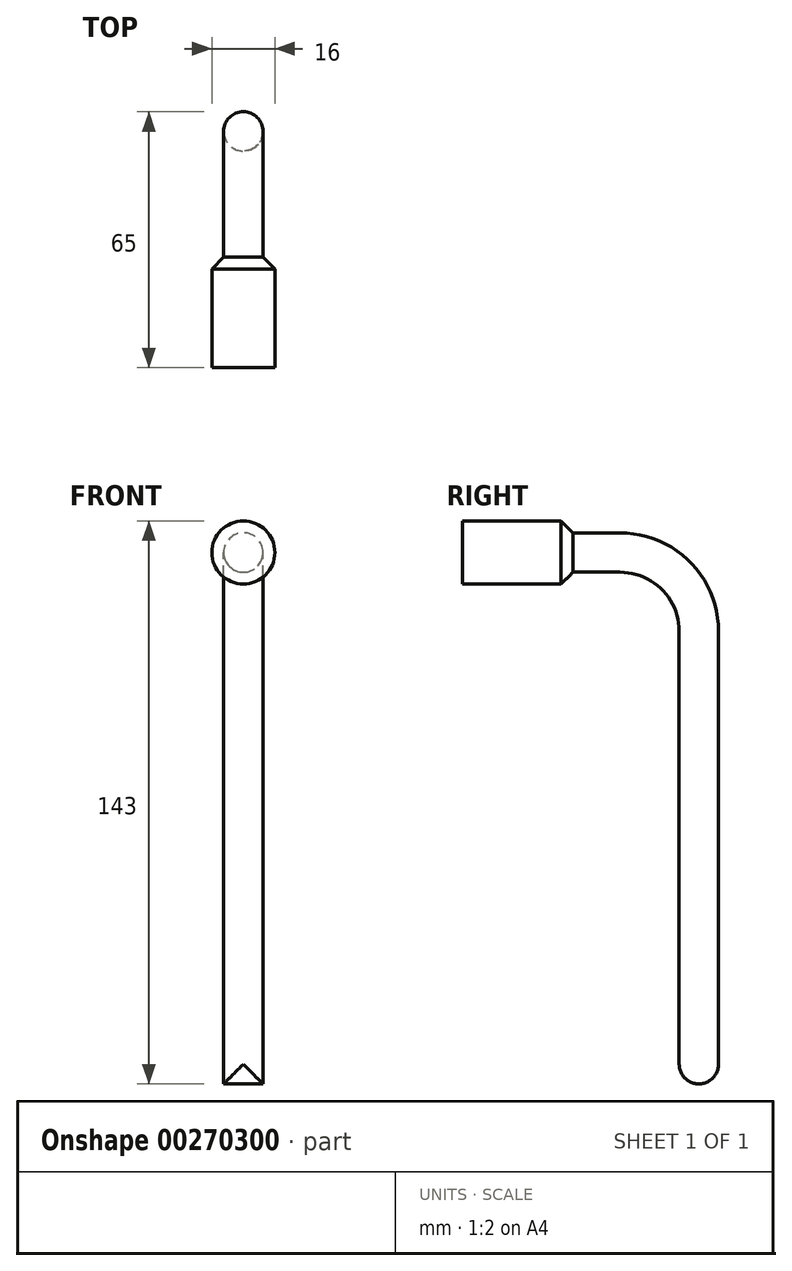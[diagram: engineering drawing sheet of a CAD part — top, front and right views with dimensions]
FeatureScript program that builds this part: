
annotation { "Feature Type Name" : "Feature", "Feature Type Description" : "" }
export const myFeature = defineFeature(function(context is Context, id is Id, definition is map)
    precondition{}
    {
        {
            var Q0;
            Q0=qCreatedBy(makeId("Front.planeOp"),FACE);
            var sketch = newSketch(context, id + "F0", { "sketchPlane" : qUnion([Q0])});
            skLineSegment(sketch, "E0", {"start": v(0, 0) * mm, "end": v(10, 0) * mm});
            skLineSegment(sketch, "E1", {"start": v(10, 0) * mm, "end": v(10, 10) * mm});
            skLineSegment(sketch, "E2", {"start": v(10, 10) * mm, "end": v(0, 10) * mm});
            skLineSegment(sketch, "E3", {"start": v(0, 10) * mm, "end": v(0, 0) * mm});
            skSolve(sketch);
        }
        {
            var Q0;
            Q0 = qSketchRegion(id + "F0", true);
            extrude(context, id + "F1", {"entities" : qUnion([Q0]), "oppositeDirection" : true, "depth" : 65 * mm});
        }
        {
            var Q0;
            Q0=makeQuery(id+"F1.opExtrude","SWEPT_FACE",FACE,{"disambiguationData":[OSD([sQuery(id+"F0.wireOp",EDGE,"E2")])]});
            var sketch = newSketch(context, id + "F2", { "sketchPlane" : qUnion([Q0])});
            skLineSegment(sketch, "E4", {"start": v(0, 65) * mm, "end": v(0, 55) * mm});
            skLineSegment(sketch, "E5", {"start": v(0, 55) * mm, "end": v(10, 55) * mm});
            skLineSegment(sketch, "E6", {"start": v(10, 55) * mm, "end": v(10, 65) * mm});
            skLineSegment(sketch, "E7", {"start": v(10, 65) * mm, "end": v(0, 65) * mm});
            skSolve(sketch);
        }
        {
            var Q0;
            Q0=makeQuery(id+"F2.imprint","IMPRINT",FACE,{"disambiguationData":[TD([[makeQuery(id+"F2.imprint","IMPRINT",EDGE,{"derivedFrom":sQuery(id+"F2.wireOp",EDGE,"E4")}),1.0]])]});
            extrude(context, id + "F3", {"entities" : qUnion([Q0]), "operationType" : NewBodyOperationType.ADD, "oppositeDirection" : true, "depth" : 140 * mm});
        }
        {
            var Q0;
            Q0=makeQuery(id+"F1.opExtrude","CAP_FACE",FACE,{"disambiguationData":[OSD([sQuery(id+"F0.wireOp",EDGE,"E0"),sQuery(id+"F0.wireOp",EDGE,"E1"),sQuery(id+"F0.wireOp",EDGE,"E2"),sQuery(id+"F0.wireOp",EDGE,"E3")])],"isStart":true});
            var sketch = newSketch(context, id + "F4", { "sketchPlane" : qUnion([Q0])});
            skLineSegment(sketch, "E8", {"start": v(0, 0) * mm, "end": v(5, 0) * mm});
            skLineSegment(sketch, "E9", {"start": v(5, 0) * mm, "end": v(5, 5) * mm});
            skCircle(sketch, "E10", {"center": v(5, 5) * mm, "radius": 8 * mm});
            skSolve(sketch);
        }
        {
            var Q0;
            {var subQ2=sQuery(id+"F4.wireOp",EDGE,"E8");Q0=makeQuery(id+"F4.imprint","IMPRINT",FACE,{"disambiguationData":[TD([[makeQuery(id+"F4.imprint","IMPRINT",EDGE,{"derivedFrom":subQ2}),-1.0]])]});}
            extrude(context, id + "F5", {"entities" : qUnion([Q0]), "operationType" : NewBodyOperationType.ADD, "oppositeDirection" : true, "depth" : 30 * mm});
        }
        {
            var Q0;
            Q0=makeQuery(id+"F3.boolean.opBoolean","INTERSECT",EDGE,{"derivedFrom":[makeQuery(id+"F1.opExtrude","SWEPT_FACE",FACE,{"disambiguationData":[OSD([sQuery(id+"F0.wireOp",EDGE,"E0")])]}),makeQuery(id+"F3.opExtrude","SWEPT_FACE",FACE,{"disambiguationData":[OSD([sQuery(id+"F2.wireOp",EDGE,"E5")])]})]});
            fillet(context, id + "F6", {"entities" : qUnion([Q0]), "radius" : 15 * mm, "tangentPropagation" : true, "allowEdgeOverflow" : false});
        }
        {
            var Q0;
            Q0=makeQuery(id+"F1.opExtrude","CAP_EDGE",EDGE,{"disambiguationData":[OSD([sQuery(id+"F0.wireOp",EDGE,"E2")])],"isStart":false});
            fillet(context, id + "F7", {"entities" : qUnion([Q0]), "radius" : 25 * mm, "tangentPropagation" : true, "allowEdgeOverflow" : false});
        }
        {
            var Q0;
            Q0=makeQuery(id+"F3.boolean.opBoolean","MERGE",FACE,{"derivedFrom":[makeQuery(id+"F1.opExtrude","CAP_FACE",FACE,{"disambiguationData":[OSD([sQuery(id+"F0.wireOp",EDGE,"E0"),sQuery(id+"F0.wireOp",EDGE,"E1"),sQuery(id+"F0.wireOp",EDGE,"E2"),sQuery(id+"F0.wireOp",EDGE,"E3")])],"isStart":false}),makeQuery(id+"F3.opExtrude","SWEPT_FACE",FACE,{"disambiguationData":[OSD([sQuery(id+"F2.wireOp",EDGE,"E7")])]})]});
            fillet(context, id + "F8", {"entities" : qUnion([Q0]), "radius" : 5 * mm, "tangentPropagation" : true, "allowEdgeOverflow" : false});
        }
        {
            var Q0;
            Q0=makeQuery(id+"F3.opExtrude","SWEPT_FACE",FACE,{"disambiguationData":[OSD([sQuery(id+"F2.wireOp",EDGE,"E5")])]});
            fillet(context, id + "F9", {"entities" : qUnion([Q0]), "radius" : 5 * mm, "tangentPropagation" : true, "allowEdgeOverflow" : false});
        }
        {
            var Q0;
            Q0=makeQuery(id+"F5.opExtrude","CAP_EDGE",EDGE,{"disambiguationData":[OSD([sQuery(id+"F4.wireOp",EDGE,"E10")])],"isStart":false});
            chamfer(context, id + "F10", {"entities" : qUnion([Q0]), "width" : 5 * mm, "tangentPropagation" : true});
        }
    });
